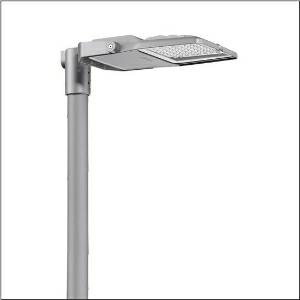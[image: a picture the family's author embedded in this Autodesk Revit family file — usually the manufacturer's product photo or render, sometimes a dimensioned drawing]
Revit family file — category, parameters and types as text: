
# Revit family: floodlight_fl_21_mini___pl64_5xa7775b2e3a_7162
name_source: partatom
category: Lighting Fixtures
units: mm (PartAtom-declared; Revit-internal decimal feet)

## family parameters
Cut with Voids When Loaded = No
Host = Face
Light Source = No
Part Type = Normal
Room Calculation Point = No
Round Connector Dimension = Use Diameter
Shared = No

## types (1)
- --- (1 x LED, 6010 lm, 45.7 W, 3000K)
    Apparent Load = 46 VA
    CIE Flux Codes = 28 80 98 100 100
    Color Rendering = 70
    Color Temperature = 3000K
    Default Elevation = 1800 mm
    Description = Floodlight FL 21 mini, floodlight, primary light control with lens, of PMMA, primary optical cover: protective disc, of toughened safety glass, transparent, light distribution: PL64, light emission: direct distribution, installation type: surface-mounted, LED, High Power LED, rated luminous flux: 6.010lm, luminous efficacy: 132lm/W, light colour: 730, colour temperature: 3000K, control gear: Smart Interface (Zhaga), control: flexible luminous flux parameterisation, time-dependent luminous flux control, constant luminous flux control, overheat protection, pre-setting: logarithmic dimming characteristic, with terminal, 6-pole, mains connection: 220..240V, AC, 50/60Hz, start of lifetime: 46W, end of service life: 48W, reduction: 22W, luminaire housing, of diecast aluminium, powder-coated, Siteco® metallic grey (DB 702S), corrosivity category C5 mid according to DIN EN ISO 12944, suitable for swimming pools, chlorine-resistant, sealing non-destructively replaceable, please order mast flange separately, mast bracket, of steel, galvanised, powder-coated, Siteco® metallic grey (DB 702S), Smart Interface above, protection rating (complete): IP66, insulation class (complete): insulation class II (safety insulation), certification: CE, ENEC, VDE, protection symbol: D, impact resistance: IK08, permissible operating ambient temperature: -40..+40°C, permissible operating ambient temperature for outdoor applications: -40..+50°C, standard: DIN EN 12944, LABS conformity tested according to VDMA 24364:2018-05, packaging unit: 1 piece

Light Distribution: PL64
    Height = 70 mm
    Lamp = 1 x LED
    Lamp Light Flux = 6010 lm
    Lamp Power = 45.7 W
    Lamp count = 1
    Length = 485 mm
    Luminous efficacy = 132 lm/W
    Manufacturer = Siteco
    ModVariant = No
    Model = 5XA7775B2E3A
    Number of Poles = 1
    OnlyDefault = Yes
    Power Factor = 1
    Product Name = Floodlight FL 21 mini | PL64
    Product group = floodlight | pylon annexe
    ProductGroupID = 6201
    Protection Class = Protection class II
    Protection Degree = IP 66
    RLX_Detail_Level = 1
    RLX_Emergency_Light_Flux = 0 lm
    RLX_Emergency_Type = 0
    RLX_Emergency_Type_DB = No
    RlxData = <blob elided: 101273 chars, md5=2b321a6b>
    Socket = socket
    Standby Power = 0 W
    System Light Flux = 6010 lm
    System Power = 46 W
    Type Comments = factory setting: luminous flux: 100 % | dim-lin: 254 | 463 mA
    Type Image = l_1007125.jpg
    URL = http://relux.com
    VarID = @adj_187009
    Voltage = 0 V
    Weight = 0.00 kg
    Width = 337 mm

## geometry (parser evidence)
native form markers: Blend x4, Sweep x12
no freeform markers — native parametric forms only
